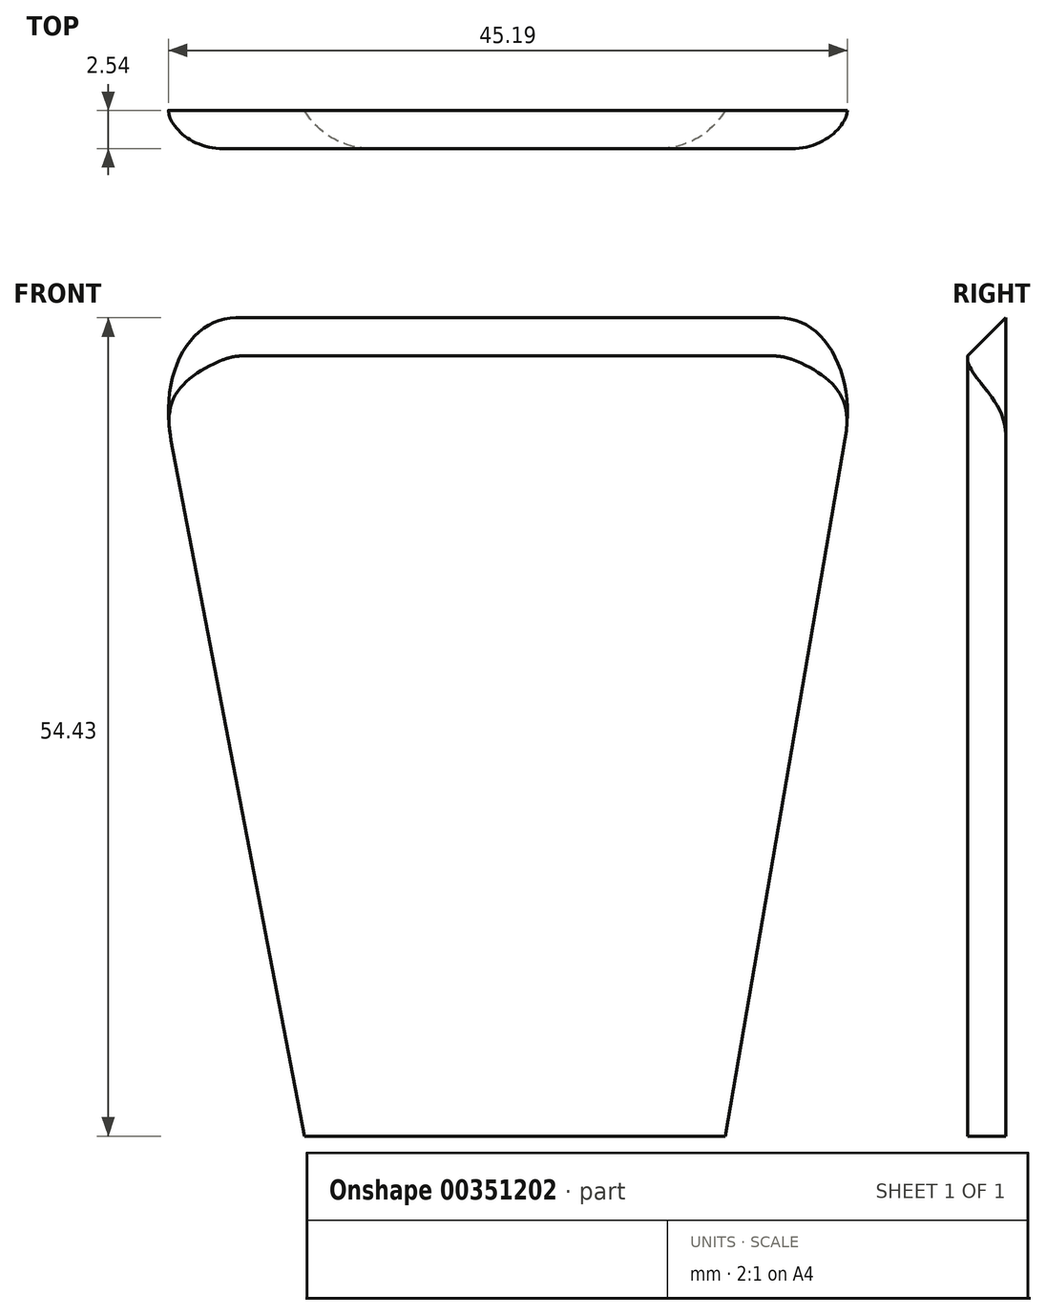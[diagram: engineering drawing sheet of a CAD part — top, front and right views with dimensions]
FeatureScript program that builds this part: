
annotation { "Feature Type Name" : "Feature", "Feature Type Description" : "" }
export const myFeature = defineFeature(function(context is Context, id is Id, definition is map)
    precondition{}
    {
        {
            var Q0;
            Q0=qCreatedBy(makeId("Front.planeOp"),FACE);
            var sketch = newSketch(context, id + "F0", { "sketchPlane" : qUnion([Q0])});
            skLineSegment(sketch, "E0", {"start": v(-51.12, 42.73) * mm, "end": v(-2.4, 42.73) * mm});
            skLineSegment(sketch, "E1", {"start": v(-2.4, 42.73) * mm, "end": v(-12.2, -14.24) * mm});
            skLineSegment(sketch, "E2", {"start": v(-12.2, -14.24) * mm, "end": v(-31.95, -14.24) * mm});
            skLineSegment(sketch, "E3", {"start": v(-31.95, -14.24) * mm, "end": v(-40.2, -14.24) * mm});
            skLineSegment(sketch, "E4", {"start": v(-40.2, -14.24) * mm, "end": v(-51.12, 42.73) * mm});
            skSolve(sketch);
        }
        {
            var Q0;
            Q0=makeQuery(id+"F0.imprint","IMPRINT",FACE,{"disambiguationData":[TD([[makeQuery(id+"F0.imprint","IMPRINT",EDGE,{"derivedFrom":sQuery(id+"F0.wireOp",EDGE,"E0")}),-1.0]])]});
            extrude(context, id + "F1", {"entities" : qUnion([Q0]), "depth" : 2.54 * mm});
        }
        {
            var Q0;
            Q0=makeQuery(id+"F1.opExtrude","CAP_EDGE",EDGE,{"disambiguationData":[OSD([sQuery(id+"F0.wireOp",EDGE,"E0")])],"isStart":false});
            chamfer(context, id + "F2", {"entities" : qUnion([Q0]), "width" : 5.08 * mm, "tangentPropagation" : true});
        }
        {
            var Q0;
            Q0=makeQuery(id+"F2.opChamfer","BLEND_EDGE",EDGE,{"blendedFrom":[makeQuery(id+"F1.opExtrude","CAP_EDGE",EDGE,{"disambiguationData":[OSD([sQuery(id+"F0.wireOp",EDGE,"E0")])],"isStart":false}),makeQuery(id+"F1.opExtrude","SWEPT_FACE",FACE,{"disambiguationData":[OSD([sQuery(id+"F0.wireOp",EDGE,"E1")])]})],"blendedInto":[makeQuery(id+"F1.opExtrude","SWEPT_FACE",FACE,{"disambiguationData":[OSD([sQuery(id+"F0.wireOp",EDGE,"E1")])]})]});
            var Q1;
            Q1=makeQuery(id+"F2.opChamfer","BLEND_EDGE",EDGE,{"blendedFrom":[makeQuery(id+"F1.opExtrude","CAP_EDGE",EDGE,{"disambiguationData":[OSD([sQuery(id+"F0.wireOp",EDGE,"E0")])],"isStart":false}),makeQuery(id+"F1.opExtrude","SWEPT_FACE",FACE,{"disambiguationData":[OSD([sQuery(id+"F0.wireOp",EDGE,"E4")])]})],"blendedInto":[makeQuery(id+"F1.opExtrude","SWEPT_FACE",FACE,{"disambiguationData":[OSD([sQuery(id+"F0.wireOp",EDGE,"E4")])]})]});
            var Q2;
            Q2=makeQuery(id+"F1.opExtrude","CAP_EDGE",EDGE,{"disambiguationData":[OSD([sQuery(id+"F0.wireOp",EDGE,"E4")])],"isStart":false});
            var Q3;
            Q3=makeQuery(id+"F1.opExtrude","CAP_EDGE",EDGE,{"disambiguationData":[OSD([sQuery(id+"F0.wireOp",EDGE,"E1")])],"isStart":false});
            fillet(context, id + "F3", {"entities" : qUnion([Q0, Q1, Q2, Q3]), "radius" : 5.08 * mm, "tangentPropagation" : true, "allowEdgeOverflow" : false});
        }
    });
